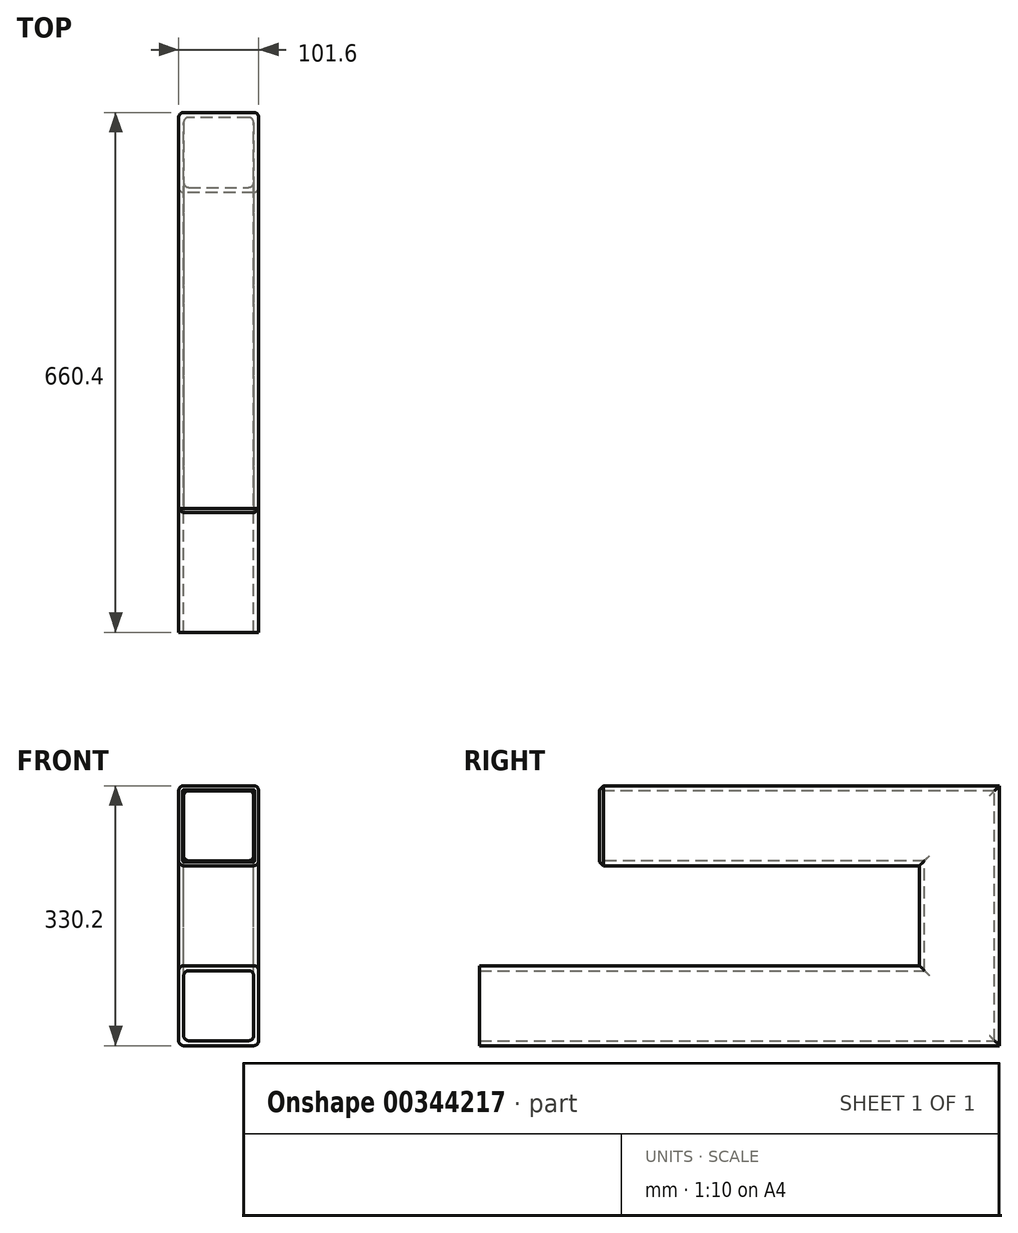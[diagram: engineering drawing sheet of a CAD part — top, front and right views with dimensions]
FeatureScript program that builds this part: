
annotation { "Feature Type Name" : "Feature", "Feature Type Description" : "" }
export const myFeature = defineFeature(function(context is Context, id is Id, definition is map)
    precondition{}
    {
        {
            var Q0;
            Q0=qCreatedBy(makeId("Front.planeOp"),FACE);
            var sketch = newSketch(context, id + "F0", { "sketchPlane" : qUnion([Q0])});
            skLineSegment(sketch, "E0.bottom", {"start": v(38.1, 44.45) * mm, "end": v(-38.1, 44.45) * mm});
            skLineSegment(sketch, "E0.top", {"start": v(38.1, -44.45) * mm, "end": v(-38.1, -44.45) * mm});
            skLineSegment(sketch, "E0.left", {"start": v(44.45, 38.1) * mm, "end": v(44.45, -38.1) * mm});
            skLineSegment(sketch, "E0.right", {"start": v(-44.45, 38.1) * mm, "end": v(-44.45, -38.1) * mm});
            skPoint(sketch, "E0.middle", {"position": v(0, 0) * mm});
            skLineSegment(sketch, "E1.bottom", {"start": v(44.45, 50.8) * mm, "end": v(-44.45, 50.8) * mm});
            skLineSegment(sketch, "E1.top", {"start": v(44.45, -50.8) * mm, "end": v(-44.45, -50.8) * mm});
            skLineSegment(sketch, "E1.left", {"start": v(50.8, 44.45) * mm, "end": v(50.8, -44.45) * mm});
            skLineSegment(sketch, "E1.right", {"start": v(-50.8, 44.45) * mm, "end": v(-50.8, -44.45) * mm});
            skPoint(sketch, "E2.visualSharp", {"position": v(-44.45, 44.45) * mm});
            skArc(sketch, "E2.filletArc", {"start": v(-38.1, 44.45) * mm, "mid": v(-42.6, 42.6) * mm, "end": v(-44.45, 38.1) * mm});
            skPoint(sketch, "E3.visualSharp", {"position": v(44.45, 44.45) * mm});
            skArc(sketch, "E3.filletArc", {"start": v(44.45, 38.1) * mm, "mid": v(42.6, 42.6) * mm, "end": v(38.1, 44.45) * mm});
            skPoint(sketch, "E4.visualSharp", {"position": v(44.45, -44.45) * mm});
            skArc(sketch, "E4.filletArc", {"start": v(38.1, -44.45) * mm, "mid": v(42.6, -42.6) * mm, "end": v(44.45, -38.1) * mm});
            skPoint(sketch, "E5.visualSharp", {"position": v(-44.45, -44.45) * mm});
            skArc(sketch, "E5.filletArc", {"start": v(-44.45, -38.1) * mm, "mid": v(-42.6, -42.6) * mm, "end": v(-38.1, -44.45) * mm});
            skPoint(sketch, "E6.visualSharp", {"position": v(-50.8, -50.8) * mm});
            skArc(sketch, "E6.filletArc", {"start": v(-50.8, -44.45) * mm, "mid": v(-48.94, -48.94) * mm, "end": v(-44.45, -50.8) * mm});
            skPoint(sketch, "E7.visualSharp", {"position": v(50.8, -50.8) * mm});
            skArc(sketch, "E7.filletArc", {"start": v(44.45, -50.8) * mm, "mid": v(48.94, -48.94) * mm, "end": v(50.8, -44.45) * mm});
            skPoint(sketch, "E8.visualSharp", {"position": v(50.8, 50.8) * mm});
            skArc(sketch, "E8.filletArc", {"start": v(50.8, 44.45) * mm, "mid": v(48.94, 48.94) * mm, "end": v(44.45, 50.8) * mm});
            skPoint(sketch, "E9.visualSharp", {"position": v(-50.8, 50.8) * mm});
            skArc(sketch, "E9.filletArc", {"start": v(-44.45, 50.8) * mm, "mid": v(-48.94, 48.94) * mm, "end": v(-50.8, 44.45) * mm});
            skSolve(sketch);
        }
        {
            var Q0;
            Q0=qCreatedBy(makeId("Right.planeOp"),FACE);
            var sketch = newSketch(context, id + "F1", { "sketchPlane" : qUnion([Q0])});
            skLineSegment(sketch, "E10", {"start": v(0, 0) * mm, "end": v(609.6, 0) * mm});
            skLineSegment(sketch, "E11", {"start": v(609.6, 0) * mm, "end": v(609.6, 228.6) * mm});
            skLineSegment(sketch, "E12", {"start": v(609.6, 228.6) * mm, "end": v(152.4, 228.6) * mm});
            skSolve(sketch);
        }
        {
            var Q0;
            Q0=makeQuery(id+"F0.imprint","IMPRINT",FACE,{"disambiguationData":[TD([[makeQuery(id+"F0.imprint","IMPRINT",EDGE,{"derivedFrom":sQuery(id+"F0.wireOp",EDGE,"E0.bottom")}),-1.0]])]});
            var Q1;
            Q1=sQuery(id+"F1.wireOp",EDGE,"E10");
            var Q2;
            Q2=sQuery(id+"F1.wireOp",EDGE,"E11");
            var Q3;
            Q3=sQuery(id+"F1.wireOp",EDGE,"E12");
            sweep(context, id + "F2", {"profiles" : qUnion([Q0]), "path" : qUnion([Q1, Q2, Q3])});
        }
        {
            var Q0;
            Q0=makeQuery(id+"F2.opSweep","CAP_EDGE",EDGE,{"disambiguationData":[OSD([sQuery(id+"F0.wireOp",EDGE,"E1.top"),sQuery(id+"F1.wireOp",VERTEX,"E12.end")])],"isStart":false});
            chamfer(context, id + "F3", {"entities" : qUnion([Q0]), "width" : 5.08 * mm, "tangentPropagation" : true});
        }
    });
